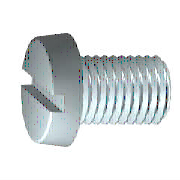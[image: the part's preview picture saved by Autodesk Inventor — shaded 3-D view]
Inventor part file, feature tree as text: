
AUTODESK INVENTOR PART (.ipt)
format: ipt  version: 2023 (Build 270158000, 158)  size: 185,344 bytes
history: native  units: mm (DEFAULTED — no unit token found)
features: sketch x2, extrude x1, plane x1
ambient origin geometry x7: Origin, YZ Plane, XZ Plane, X Axis, Y Axis, Z Axis, Center Point
bodies: Solid1 (feature_tree), Body (feature_tree)
feature tree (4):
  sketch  "Sketch2"  dims[d2=0.49086mm d3=3.3mm d4=5.0mm d5=4.566987mm d8=90.0deg d7=0.0mm d9=8.5mm d10=0.872665mm d11=1.2mm d12=8.5mm d14=0.2mm d15=8.4mm d16=0.0mm d17=0.433015mm d18=0.49086mm d19=1.3mm d20=0.0mm d36=45.0deg d37=0.0mm d39=0.0mm]
  extrude  "Slot"  Depth=10.0mm
  plane  "Work Plane1"
  sketch  "Sketch1"  dims[d0=10.0mm d1=8.4mm]
